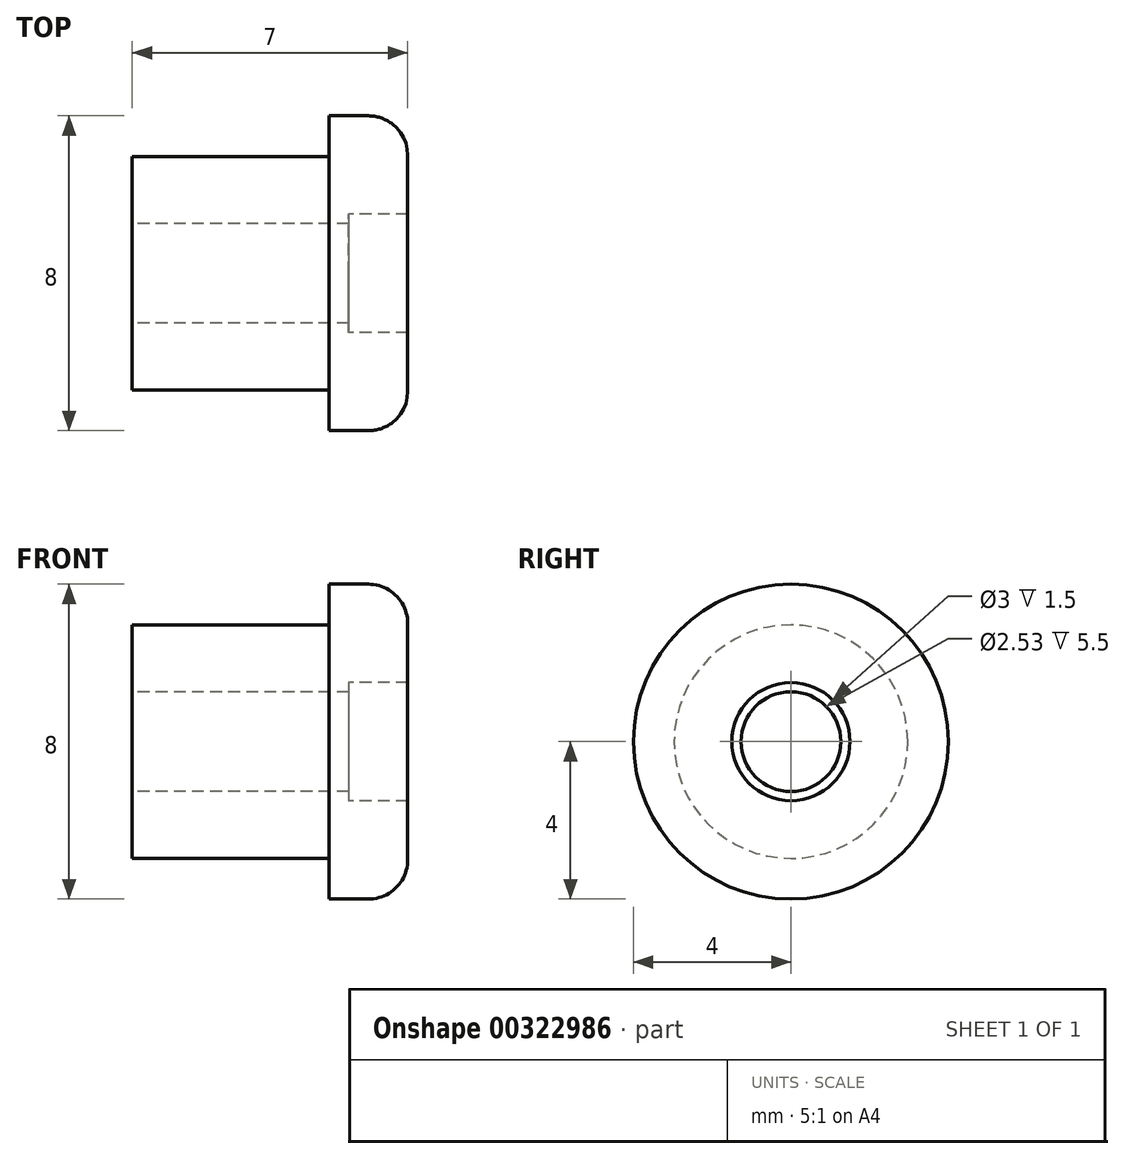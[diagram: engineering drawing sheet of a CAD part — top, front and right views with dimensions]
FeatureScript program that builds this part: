
annotation { "Feature Type Name" : "Feature", "Feature Type Description" : "" }
export const myFeature = defineFeature(function(context is Context, id is Id, definition is map)
    precondition{}
    {
        {
            var Q0;
            Q0=qCreatedBy(makeId("Front.planeOp"),FACE);
            var sketch = newSketch(context, id + "F0", { "sketchPlane" : qUnion([Q0])});
            skLineSegment(sketch, "E0", {"start": v(0, 0) * mm, "end": v(8.37, 0) * mm, "construction": true});
            skLineSegment(sketch, "E1", {"start": v(0, 0) * mm, "end": v(0, 1.5) * mm, "construction": true});
            skLineSegment(sketch, "E2", {"start": v(0, 1.5) * mm, "end": v(1.5, 1.5) * mm});
            skLineSegment(sketch, "E3", {"start": v(1.5, 1.5) * mm, "end": v(1.5, 4) * mm});
            skLineSegment(sketch, "E4", {"start": v(1.5, 4) * mm, "end": v(-0.5, 4) * mm});
            skLineSegment(sketch, "E5", {"start": v(-0.5, 4) * mm, "end": v(-0.5, 0) * mm, "construction": true});
            skLineSegment(sketch, "E6", {"start": v(-0.5, 0) * mm, "end": v(-0.5, 2.97) * mm, "construction": true});
            skLineSegment(sketch, "E7", {"start": v(-0.5, 4) * mm, "end": v(-0.5, 2.97) * mm});
            skLineSegment(sketch, "E8", {"start": v(-0.5, 2.97) * mm, "end": v(-5.5, 2.97) * mm});
            skLineSegment(sketch, "E9", {"start": v(-5.5, 2.97) * mm, "end": v(-5.5, 1.27) * mm});
            skLineSegment(sketch, "E10", {"start": v(-5.5, 1.27) * mm, "end": v(0, 1.27) * mm});
            skLineSegment(sketch, "E11", {"start": v(0, 1.27) * mm, "end": v(0, 1.5) * mm});
            skSolve(sketch);
        }
        {
            var Q0;
            Q0=makeQuery(id+"F0.imprint","IMPRINT",FACE,{"disambiguationData":[TD([[makeQuery(id+"F0.imprint","IMPRINT",EDGE,{"derivedFrom":sQuery(id+"F0.wireOp",EDGE,"E2")}),1.0]])]});
            var Q1;
            Q1=sQuery(id+"F0.wireOp",EDGE,"E0");
            revolve(context, id + "F1", {"entities" : qUnion([Q0]), "axis" : qUnion([Q1]), "revolveType" : RevolveType.FULL});
        }
        {
            var Q0;
            Q0=makeQuery(id+"F1.opRevolve","SWEPT_EDGE",EDGE,{"disambiguationData":[OSD([sQuery(id+"F0.wireOp",EDGE,"E3"),sQuery(id+"F0.wireOp",EDGE,"E4")])]});
            fillet(context, id + "F2", {"entities" : qUnion([Q0]), "radius" : 1 * mm, "tangentPropagation" : true, "allowEdgeOverflow" : false});
        }
    });
